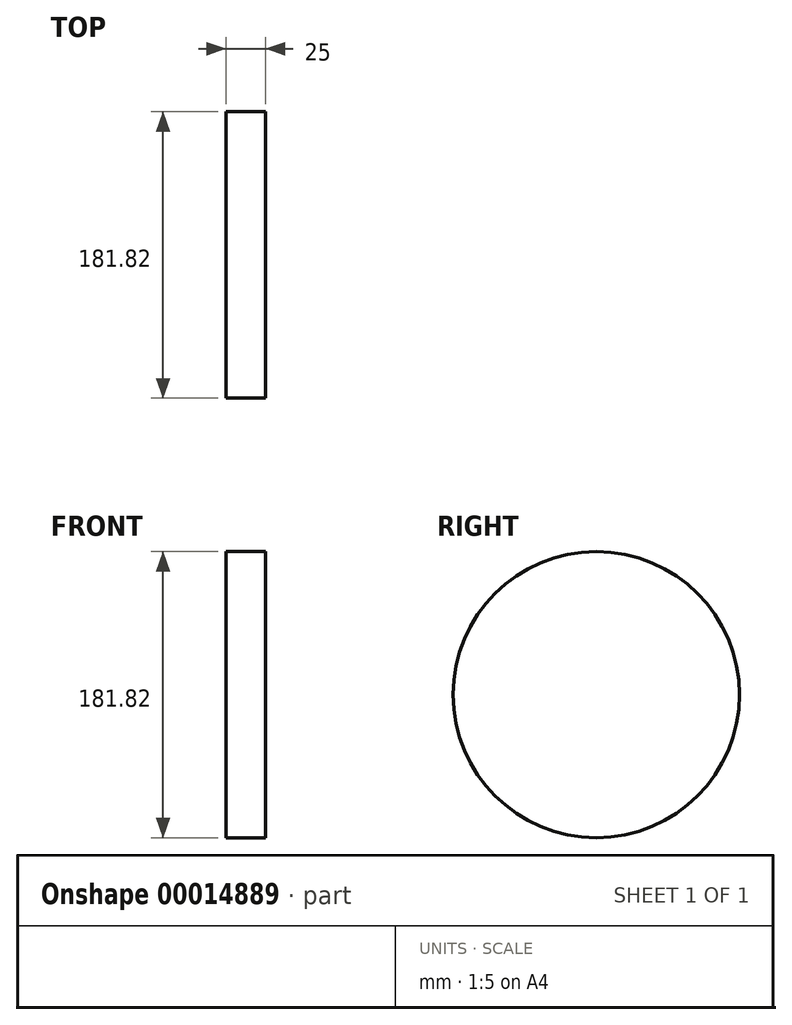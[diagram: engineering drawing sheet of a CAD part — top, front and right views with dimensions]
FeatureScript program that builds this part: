
annotation { "Feature Type Name" : "Feature", "Feature Type Description" : "" }
export const myFeature = defineFeature(function(context is Context, id is Id, definition is map)
    precondition{}
    {
        {
            var Q0;
            Q0=qCreatedBy(makeId("Right.planeOp"),FACE);
            var sketch = newSketch(context, id + "F0", { "sketchPlane" : qUnion([Q0])});
            skCircle(sketch, "E0", {"center": v(0, 0) * mm, "radius": 90.91 * mm});
            skLineSegment(sketch, "E1", {"start": v(-73.85, 107.19) * mm, "end": v(-204.08, 72.83) * mm});
            skLineSegment(sketch, "E2", {"start": v(-204.08, 72.83) * mm, "end": v(-194.78, 126.64) * mm});
            skLineSegment(sketch, "E3", {"start": v(-194.78, 126.64) * mm, "end": v(-77.5, -116.08) * mm});
            skSolve(sketch);
        }
        {
            var Q0;
            Q0 = qSketchRegion(id + "F0", true);
            var Q1;
            Q1=sQuery(id+"F0.wireOp",EDGE,"E0");
            extrude(context, id + "F1", {"entities" : qUnion([Q0]), "bodyType" : ToolBodyType.SURFACE, "surfaceEntities" : qUnion([Q1]), "depth" : 25 * mm});
        }
    });
